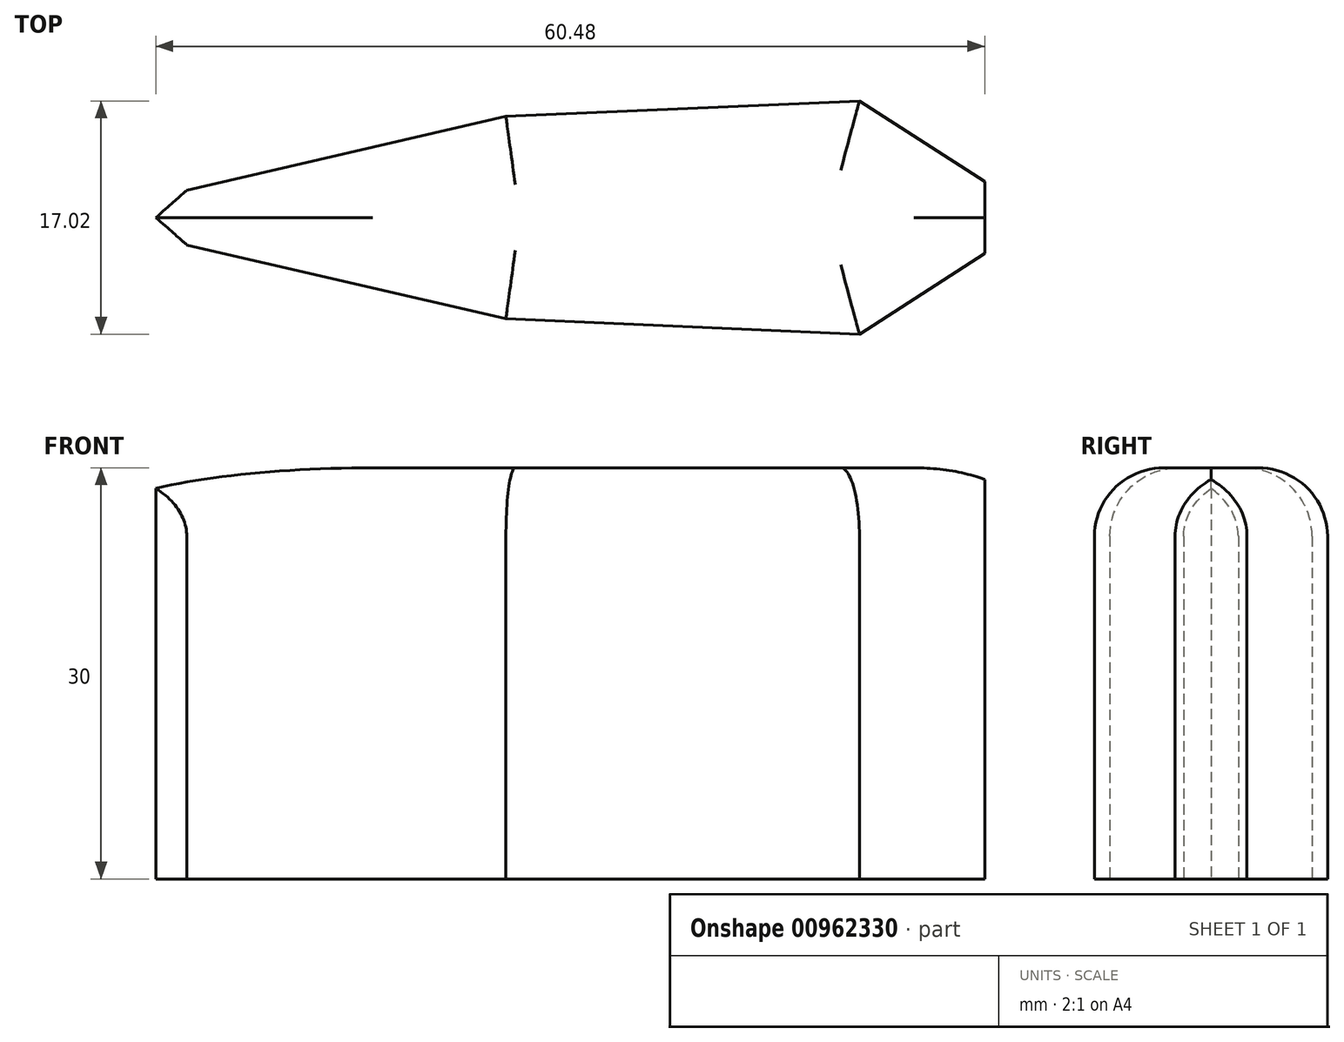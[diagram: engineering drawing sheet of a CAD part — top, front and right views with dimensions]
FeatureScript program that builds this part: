
annotation { "Feature Type Name" : "Feature", "Feature Type Description" : "" }
export const myFeature = defineFeature(function(context is Context, id is Id, definition is map)
    precondition{}
    {
        {
            var Q0;
            Q0=qCreatedBy(makeId("Top.planeOp"),FACE);
            var sketch = newSketch(context, id + "F0", { "sketchPlane" : qUnion([Q0])});
            skLineSegment(sketch, "E0", {"start": v(-45.95, 0) * mm, "end": v(-35.94, 9.27) * mm});
            skLineSegment(sketch, "E1", {"start": v(-35.94, 9.27) * mm, "end": v(-10.14, 15.03) * mm});
            skLineSegment(sketch, "E2", {"start": v(-10.14, 15.03) * mm, "end": v(20.91, 17.28) * mm});
            skLineSegment(sketch, "E3", {"start": v(20.91, 17.28) * mm, "end": v(27.17, 9.27) * mm});
            skLineSegment(sketch, "E4", {"start": v(27.17, 9.27) * mm, "end": v(43.7, 0) * mm});
            skLineSegment(sketch, "E5", {"start": v(16.99, 8.5) * mm, "end": v(-8.8, 7.38) * mm});
            skLineSegment(sketch, "E6", {"start": v(-8.8, 7.38) * mm, "end": v(-32.1, 2) * mm});
            skLineSegment(sketch, "E7", {"start": v(-32.1, 2) * mm, "end": v(-34.35, 0) * mm});
            skLineSegment(sketch, "E8", {"start": v(16.99, 8.5) * mm, "end": v(26.13, 2.62) * mm});
            skLineSegment(sketch, "E9", {"start": v(26.13, 2.62) * mm, "end": v(26.13, 0) * mm});
            skLineSegment(sketch, "E10.MirrorCS", {"start": v(-45.95, 0) * mm, "end": v(-35.94, -9.27) * mm});
            skLineSegment(sketch, "E11.MirrorCS", {"start": v(-35.94, -9.27) * mm, "end": v(-10.14, -15.03) * mm});
            skLineSegment(sketch, "E12.MirrorCS", {"start": v(-10.14, -15.03) * mm, "end": v(20.91, -17.28) * mm});
            skLineSegment(sketch, "E13.MirrorCS", {"start": v(20.91, -17.28) * mm, "end": v(27.17, -9.27) * mm});
            skLineSegment(sketch, "E14.MirrorCS", {"start": v(27.17, -9.27) * mm, "end": v(43.7, 0) * mm});
            skLineSegment(sketch, "E15.MirrorCS", {"start": v(-32.1, -2) * mm, "end": v(-34.35, 0) * mm});
            skLineSegment(sketch, "E16.MirrorCS", {"start": v(-8.8, -7.38) * mm, "end": v(-32.1, -2) * mm});
            skLineSegment(sketch, "E17.MirrorCS", {"start": v(16.99, -8.5) * mm, "end": v(-8.8, -7.38) * mm});
            skLineSegment(sketch, "E18.MirrorCS", {"start": v(16.99, -8.5) * mm, "end": v(26.13, -2.62) * mm});
            skLineSegment(sketch, "E19.MirrorCS", {"start": v(26.13, -2.62) * mm, "end": v(26.13, 0) * mm});
            skSolve(sketch);
        }
        {
            var Q0;
            Q0=makeQuery(id+"F0.imprint","IMPRINT",FACE,{"disambiguationData":[TD([[makeQuery(id+"F0.imprint","IMPRINT",EDGE,{"derivedFrom":sQuery(id+"F0.wireOp",EDGE,"E5")}),1.0]])]});
            extrude(context, id + "F1", {"entities" : qUnion([Q0]), "depth" : 30 * mm, "offsetDistance" : 25 * mm});
        }
        {
            var Q0;
            Q0=makeQuery(id+"F1.opExtrude","CAP_EDGE",EDGE,{"disambiguationData":[OSD([sQuery(id+"F0.wireOp",EDGE,"E17.MirrorCS")])],"isStart":false});
            var Q1;
            Q1=makeQuery(id+"F1.opExtrude","CAP_EDGE",EDGE,{"disambiguationData":[OSD([sQuery(id+"F0.wireOp",EDGE,"E5")])],"isStart":false});
            var Q2;
            Q2=makeQuery(id+"F1.opExtrude","CAP_EDGE",EDGE,{"disambiguationData":[OSD([sQuery(id+"F0.wireOp",EDGE,"E16.MirrorCS")])],"isStart":false});
            var Q3;
            Q3=makeQuery(id+"F1.opExtrude","CAP_FACE",FACE,{"disambiguationData":[OSD([sQuery(id+"F0.wireOp",EDGE,"E5"),sQuery(id+"F0.wireOp",EDGE,"E6"),sQuery(id+"F0.wireOp",EDGE,"E7"),sQuery(id+"F0.wireOp",EDGE,"E8"),sQuery(id+"F0.wireOp",EDGE,"E9"),sQuery(id+"F0.wireOp",EDGE,"E15.MirrorCS"),sQuery(id+"F0.wireOp",EDGE,"E16.MirrorCS"),sQuery(id+"F0.wireOp",EDGE,"E17.MirrorCS"),sQuery(id+"F0.wireOp",EDGE,"E18.MirrorCS"),sQuery(id+"F0.wireOp",EDGE,"E19.MirrorCS")])],"isStart":false});
            fillet(context, id + "F2", {"entities" : qUnion([Q0, Q1, Q2, Q3]), "radius" : 5 * mm, "tangentPropagation" : true, "allowEdgeOverflow" : false});
        }
    });
